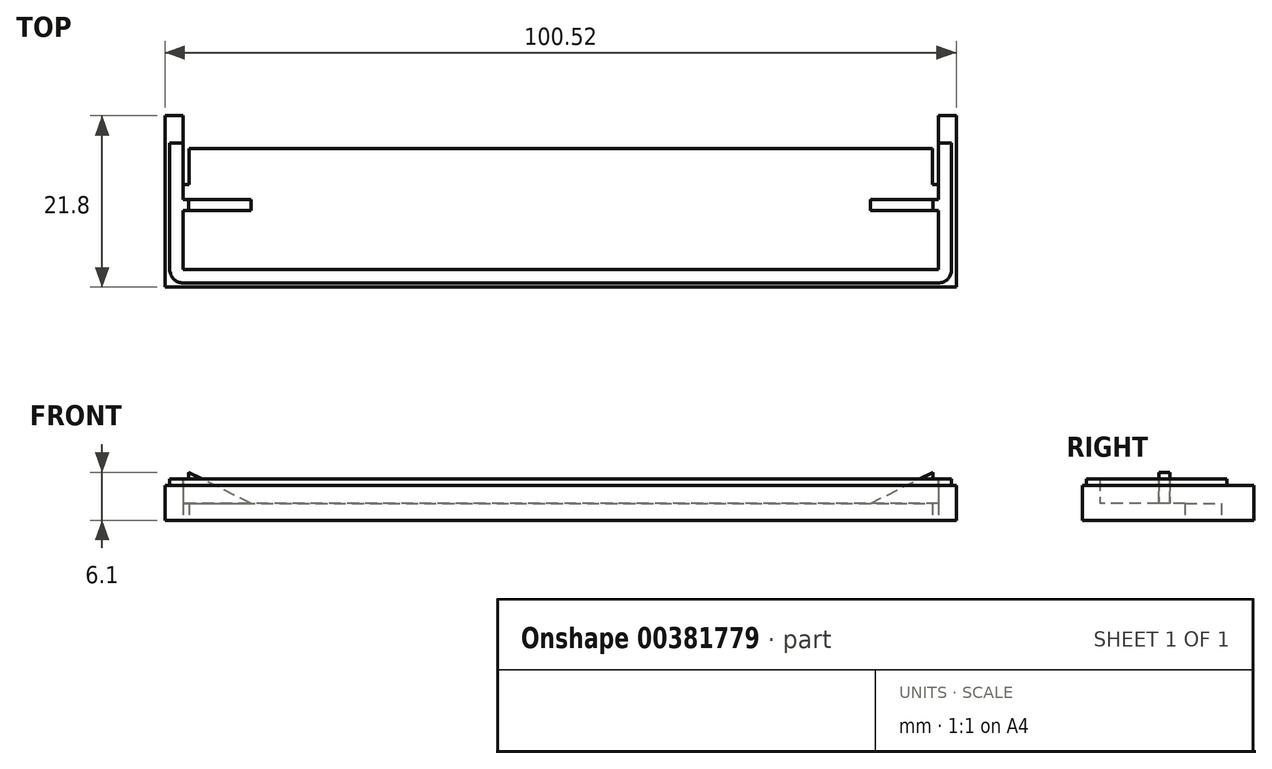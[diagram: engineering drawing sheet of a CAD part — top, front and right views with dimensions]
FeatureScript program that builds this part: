
annotation { "Feature Type Name" : "Feature", "Feature Type Description" : "" }
export const myFeature = defineFeature(function(context is Context, id is Id, definition is map)
    precondition{}
    {
        {
            var Q0;
            Q0=qCreatedBy(makeId("Top.planeOp"),FACE);
            var sketch = newSketch(context, id + "F0", { "sketchPlane" : qUnion([Q0])});
            skLineSegment(sketch, "E0.bottom", {"start": v(0, -11.26) * mm, "end": v(50.26, -11.26) * mm});
            skLineSegment(sketch, "E0.top", {"start": v(47.96, 10.54) * mm, "end": v(50.26, 10.54) * mm});
            skLineSegment(sketch, "E0.right", {"start": v(50.26, -11.26) * mm, "end": v(50.26, 10.54) * mm});
            skLineSegment(sketch, "E1", {"start": v(47.96, 10.54) * mm, "end": v(47.96, 1.8) * mm});
            skLineSegment(sketch, "E2", {"start": v(47.96, 1.8) * mm, "end": v(47.2, 1.8) * mm});
            skLineSegment(sketch, "E3", {"start": v(47.2, 1.8) * mm, "end": v(47.2, 6.4) * mm});
            skLineSegment(sketch, "E4", {"start": v(47.2, 6.4) * mm, "end": v(0, 6.4) * mm});
            skLineSegment(sketch, "E5", {"start": v(0, 6.4) * mm, "end": v(0, -11.26) * mm});
            skLineSegment(sketch, "E6", {"start": v(0, 20.1) * mm, "end": v(0, -22.02) * mm, "construction": true});
            skLineSegment(sketch, "E7.MirrorCS", {"start": v(-47.96, 1.8) * mm, "end": v(-47.2, 1.8) * mm});
            skLineSegment(sketch, "E8.MirrorCS", {"start": v(-50.26, -11.26) * mm, "end": v(-50.26, 10.54) * mm});
            skLineSegment(sketch, "E9.MirrorCS", {"start": v(-47.96, 10.54) * mm, "end": v(-50.26, 10.54) * mm});
            skLineSegment(sketch, "E10.MirrorCS", {"start": v(-47.96, 10.54) * mm, "end": v(-47.96, 1.8) * mm});
            skLineSegment(sketch, "E11.MirrorCS", {"start": v(-47.2, 1.8) * mm, "end": v(-47.2, 6.4) * mm});
            skLineSegment(sketch, "E12.MirrorCS", {"start": v(0, -11.26) * mm, "end": v(-50.26, -11.26) * mm});
            skLineSegment(sketch, "E13.MirrorCS", {"start": v(-47.2, 6.4) * mm, "end": v(0, 6.4) * mm});
            skSolve(sketch);
        }
        {
            var Q0;
            Q0=makeQuery(id+"F0.imprint","IMPRINT",FACE,{"disambiguationData":[TD([[makeQuery(id+"F0.imprint","IMPRINT",EDGE,{"derivedFrom":sQuery(id+"F0.wireOp",EDGE,"E5")}),-1.0]])]});
            var Q1;
            Q1=makeQuery(id+"F0.imprint","IMPRINT",FACE,{"disambiguationData":[TD([[makeQuery(id+"F0.imprint","IMPRINT",EDGE,{"derivedFrom":sQuery(id+"F0.wireOp",EDGE,"E0.bottom")}),1.0]])]});
            extrude(context, id + "F1", {"entities" : qUnion([Q0, Q1]), "depth" : 2.15 * mm});
        }
        {
            var Q0;
            Q0=makeQuery(id+"F1.opExtrude","CAP_FACE",FACE,{"disambiguationData":[OSD([sQuery(id+"F0.wireOp",EDGE,"E0.bottom"),sQuery(id+"F0.wireOp",EDGE,"E0.top"),sQuery(id+"F0.wireOp",EDGE,"E0.right"),sQuery(id+"F0.wireOp",EDGE,"E1"),sQuery(id+"F0.wireOp",EDGE,"E2"),sQuery(id+"F0.wireOp",EDGE,"E3"),sQuery(id+"F0.wireOp",EDGE,"E4"),sQuery(id+"F0.wireOp",EDGE,"E7.MirrorCS"),sQuery(id+"F0.wireOp",EDGE,"E8.MirrorCS"),sQuery(id+"F0.wireOp",EDGE,"E9.MirrorCS"),sQuery(id+"F0.wireOp",EDGE,"E10.MirrorCS"),sQuery(id+"F0.wireOp",EDGE,"E11.MirrorCS"),sQuery(id+"F0.wireOp",EDGE,"E12.MirrorCS"),sQuery(id+"F0.wireOp",EDGE,"E13.MirrorCS")])],"isStart":false});
            var sketch = newSketch(context, id + "F2", { "sketchPlane" : qUnion([Q0])});
            skLineSegment(sketch, "E14", {"start": v(-47.96, 1.8) * mm, "end": v(-47.96, -9) * mm});
            skLineSegment(sketch, "E15", {"start": v(-47.96, -9) * mm, "end": v(0, -9) * mm});
            skLineSegment(sketch, "E16", {"start": v(0, 11.08) * mm, "end": v(0, -13.14) * mm, "construction": true});
            skLineSegment(sketch, "E17.MirrorCS", {"start": v(47.96, 1.8) * mm, "end": v(47.96, -9) * mm});
            skLineSegment(sketch, "E18.MirrorCS", {"start": v(47.96, -9) * mm, "end": v(0, -9) * mm});
            skSolve(sketch);
        }
        {
            var Q0;
            Q0=makeQuery(id+"F2.imprint","IMPRINT",FACE,{"disambiguationData":[TD([[makeQuery(id+"F2.imprint","IMPRINT",EDGE,{"derivedFrom":sQuery(id+"F2.wireOp",EDGE,"E14")}),-1.0]])]});
            extrude(context, id + "F3", {"entities" : qUnion([Q0]), "operationType" : NewBodyOperationType.ADD, "depth" : 3.1 * mm});
        }
        {
            var Q0;
            Q0=makeQuery(id+"F3.opExtrude","CAP_FACE",FACE,{"disambiguationData":[OSD([sQuery(id+"F0.wireOp",EDGE,"E0.bottom"),sQuery(id+"F0.wireOp",EDGE,"E0.top"),sQuery(id+"F0.wireOp",EDGE,"E0.right"),sQuery(id+"F0.wireOp",EDGE,"E1"),sQuery(id+"F0.wireOp",EDGE,"E8.MirrorCS"),sQuery(id+"F0.wireOp",EDGE,"E9.MirrorCS"),sQuery(id+"F0.wireOp",EDGE,"E10.MirrorCS"),sQuery(id+"F0.wireOp",EDGE,"E12.MirrorCS"),sQuery(id+"F2.wireOp",EDGE,"E14"),sQuery(id+"F2.wireOp",EDGE,"E15"),sQuery(id+"F2.wireOp",EDGE,"E17.MirrorCS"),sQuery(id+"F2.wireOp",EDGE,"E18.MirrorCS")])],"isStart":false});
            var sketch = newSketch(context, id + "F4", { "sketchPlane" : qUnion([Q0])});
            skLineSegment(sketch, "E19", {"start": v(-49.66, 7.1) * mm, "end": v(-49.66, -9) * mm});
            skLineSegment(sketch, "E20", {"start": v(-47.96, -10.7) * mm, "end": v(0, -10.7) * mm});
            skPoint(sketch, "E21", {"position": v(-49.66, -9) * mm});
            skPoint(sketch, "E22", {"position": v(-47.96, -10.7) * mm});
            skArc(sketch, "E23", {"start": v(-47.96, -10.7) * mm, "mid": v(-49.16, -10.21) * mm, "end": v(-49.66, -9) * mm});
            skLineSegment(sketch, "E24", {"start": v(-49.66, 7.1) * mm, "end": v(-47.96, 7.1) * mm});
            skLineSegment(sketch, "E25", {"start": v(0, 10.22) * mm, "end": v(0, -15.62) * mm, "construction": true});
            skPoint(sketch, "E25.endSnap0", {"position": v(0, -11.26) * mm});
            skLineSegment(sketch, "E26.MirrorCS", {"start": v(47.96, -10.7) * mm, "end": v(0, -10.7) * mm});
            skLineSegment(sketch, "E27.MirrorCS", {"start": v(49.66, 7.1) * mm, "end": v(49.66, -9) * mm});
            skArc(sketch, "E28.MirrorCS", {"start": v(47.96, -10.7) * mm, "mid": v(49.16, -10.21) * mm, "end": v(49.66, -9) * mm});
            skLineSegment(sketch, "E29.MirrorCS", {"start": v(49.66, 7.1) * mm, "end": v(47.96, 7.1) * mm});
            skSolve(sketch);
        }
        {
            var Q0;
            Q0=makeQuery(id+"F4.imprint","IMPRINT",FACE,{"disambiguationData":[TD([[makeQuery(id+"F4.imprint","IMPRINT",EDGE,{"derivedFrom":sQuery(id+"F4.wireOp",EDGE,"E19")}),-1.0]])]});
            extrude(context, id + "F5", {"entities" : qUnion([Q0]), "operationType" : NewBodyOperationType.REMOVE, "oppositeDirection" : true, "depth" : 0.8 * mm});
        }
        {
            var Q0;
            Q0=makeQuery(id+"F1.opExtrude","CAP_FACE",FACE,{"disambiguationData":[OSD([sQuery(id+"F0.wireOp",EDGE,"E0.bottom"),sQuery(id+"F0.wireOp",EDGE,"E0.top"),sQuery(id+"F0.wireOp",EDGE,"E0.right"),sQuery(id+"F0.wireOp",EDGE,"E1"),sQuery(id+"F0.wireOp",EDGE,"E2"),sQuery(id+"F0.wireOp",EDGE,"E3"),sQuery(id+"F0.wireOp",EDGE,"E4"),sQuery(id+"F0.wireOp",EDGE,"E7.MirrorCS"),sQuery(id+"F0.wireOp",EDGE,"E8.MirrorCS"),sQuery(id+"F0.wireOp",EDGE,"E9.MirrorCS"),sQuery(id+"F0.wireOp",EDGE,"E10.MirrorCS"),sQuery(id+"F0.wireOp",EDGE,"E11.MirrorCS"),sQuery(id+"F0.wireOp",EDGE,"E12.MirrorCS"),sQuery(id+"F0.wireOp",EDGE,"E13.MirrorCS")])],"isStart":false});
            var sketch = newSketch(context, id + "F6", { "sketchPlane" : qUnion([Q0])});
            skLineSegment(sketch, "E30", {"start": v(-47.96, -1.5) * mm, "end": v(-39.36, -1.5) * mm});
            skSolve(sketch);
        }
        {
            var Q0;
            Q0=makeQuery(id+"F3.opExtrude","SWEPT_FACE",FACE,{"disambiguationData":[OSD([sQuery(id+"F2.wireOp",EDGE,"E15"),sQuery(id+"F2.wireOp",EDGE,"E18.MirrorCS")])]});
            var Q1;
            Q1=sQuery(id+"F6.wireOp",VERTEX,"E30.end");
            cPlane(context, id + "F7", {"entities" : qUnion([Q0, Q1]), "cplaneType" : CPlaneType.PLANE_POINT, "offset" : 25 * mm, "width" : 150 * mm, "height" : 150 * mm});
        }
        {
            var Q0;
            Q0=qCreatedBy(id+"F7.planeOp",FACE);
            var sketch = newSketch(context, id + "F8", { "sketchPlane" : qUnion([Q0])});
            skPoint(sketch, "E31.0", {"position": v(39.36, 2.15) * mm});
            skLineSegment(sketch, "E32", {"start": v(39.36, 2.15) * mm, "end": v(47.26, 6.1) * mm});
            skLineSegment(sketch, "E33", {"start": v(47.26, 6.1) * mm, "end": v(47.26, 5.25) * mm});
            skLineSegment(sketch, "E34", {"start": v(47.26, 5.25) * mm, "end": v(47.96, 5.25) * mm});
            skLineSegment(sketch, "E35", {"start": v(47.96, 5.25) * mm, "end": v(47.96, 2.15) * mm});
            skLineSegment(sketch, "E36", {"start": v(47.96, 2.15) * mm, "end": v(39.36, 2.15) * mm});
            skSolve(sketch);
        }
        {
            var Q0;
            Q0=makeQuery(id+"F8.imprint","IMPRINT",FACE,{"disambiguationData":[TD([[makeQuery(id+"F8.imprint","IMPRINT",EDGE,{"derivedFrom":sQuery(id+"F8.wireOp",EDGE,"E32")}),-1.0]])]});
            extrude(context, id + "F9", {"entities" : qUnion([Q0]), "operationType" : NewBodyOperationType.ADD, "depth" : 1.4 * mm});
        }
        {
            var Q0;
            Q0=makeQuery(id+"F1.opExtrude","SWEPT_BODY",BODY,{"disambiguationData":[OSD([sQuery(id+"F0.wireOp",EDGE,"E0.bottom"),sQuery(id+"F0.wireOp",EDGE,"E0.top"),sQuery(id+"F0.wireOp",EDGE,"E0.right"),sQuery(id+"F0.wireOp",EDGE,"E1"),sQuery(id+"F0.wireOp",EDGE,"E2"),sQuery(id+"F0.wireOp",EDGE,"E3"),sQuery(id+"F0.wireOp",EDGE,"E4"),sQuery(id+"F0.wireOp",EDGE,"E7.MirrorCS"),sQuery(id+"F0.wireOp",EDGE,"E8.MirrorCS"),sQuery(id+"F0.wireOp",EDGE,"E9.MirrorCS"),sQuery(id+"F0.wireOp",EDGE,"E10.MirrorCS"),sQuery(id+"F0.wireOp",EDGE,"E11.MirrorCS"),sQuery(id+"F0.wireOp",EDGE,"E12.MirrorCS"),sQuery(id+"F0.wireOp",EDGE,"E13.MirrorCS")])]});
            var Q1;
            Q1=qCreatedBy(makeId("Right.planeOp"),FACE);
            mirror(context, id + "F10", {"operationType" : NewBodyOperationType.ADD, "entities" : qUnion([Q0]), "mirrorPlane" : qUnion([Q1])});
        }
    });
